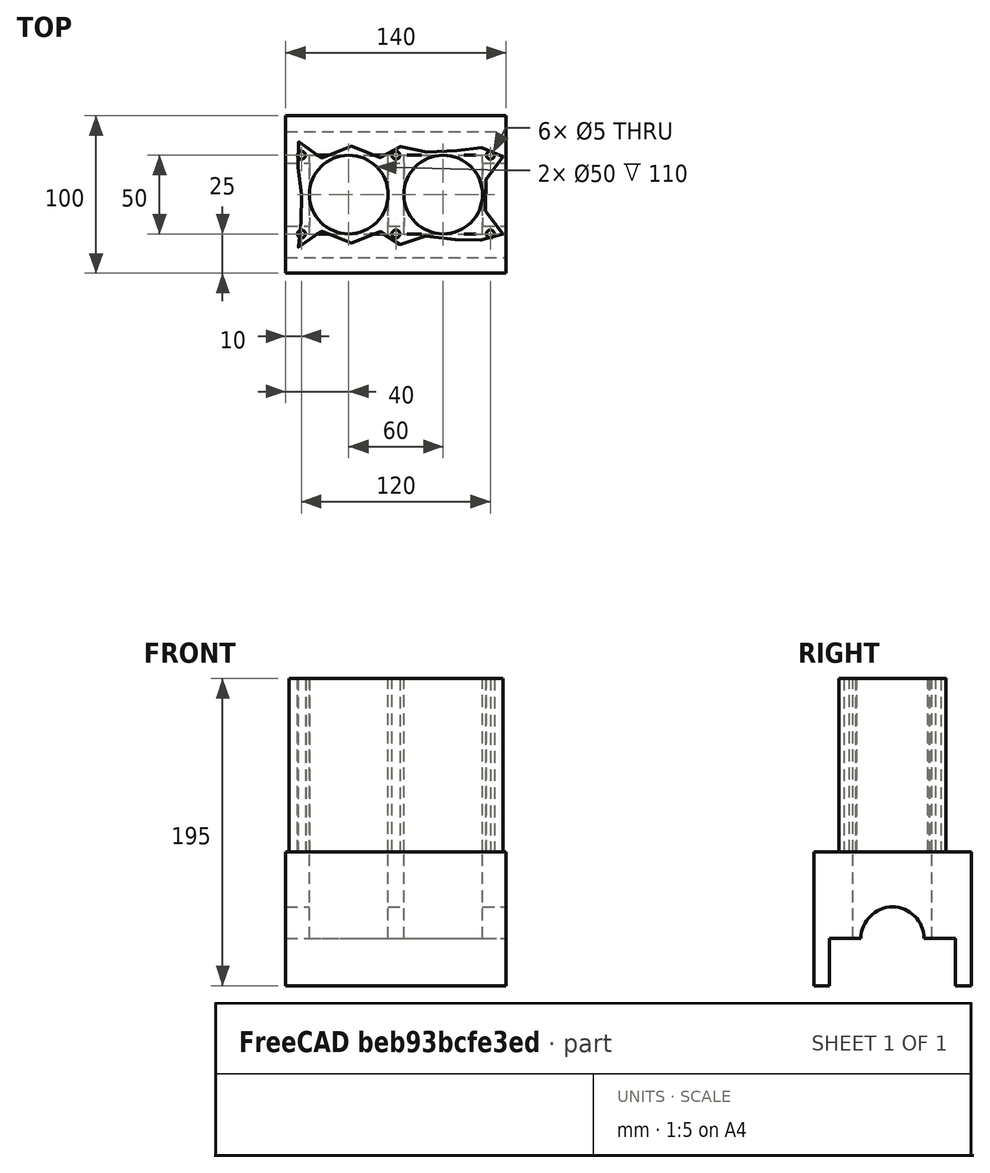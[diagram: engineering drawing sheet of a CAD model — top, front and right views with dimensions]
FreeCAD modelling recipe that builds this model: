
FCSTD DOCUMENT  (FreeCAD 0.19R17171 (Git))
Label: EngineBlock
License: Creative Commons Attribution-ShareAlike
LicenseURL: https://creativecommons.org/licenses/by-sa/4.0/
objects: Part::Part2DObjectPython×8, Part::Extrusion×7, Part::Box×5, Part::Cut×5, Part::Cylinder×3, Part::MultiFuse×3, Part::Mirroring×3, App::DocumentObjectGroup×1, Part::MultiCommon×1
note: 35 computed .brp shape members not serialized (recipe doc carries the construction recipe); baked Part::Feature solids carry a one-line shape summary decoded from their .brp

FEATURE [Part::Box] Box  label="Billet"
  AttacherType = Attacher::AttachEngine3D
  Height = 110
  Length = 140
  Placement = pos=(0,-40,0) rot=(0,0,1;0rad)
  Width = 80
FEATURE [Part::Cylinder] Cylinder  label="Cylinder 1"
  Angle = 360
  AttacherType = Attacher::AttachEngine3D
  Height = 110
  Placement = pos=(40,0,0) rot=(0,0,1;0rad)
  Radius = 25
FEATURE [Part::Cylinder] Cylinder001  label="Cylinder 2"
  Angle = 360
  AttacherType = Attacher::AttachEngine3D
  Height = 110
  Placement = pos=(100,0,0) rot=(0,0,1;0rad)
  Radius = 25
FEATURE [Part::MultiFuse] Fusion  label="Cylinders"
  Shapes = -> [Cylinder,Cylinder001]
FEATURE [Part::Cut] Cut  label="Bored Block"
  Base = -> Box
  Tool = -> Fusion
FEATURE [Part::Box] Box001  label="Crankcase Billet"
  AttacherType = Attacher::AttachEngine3D
  Height = 85
  Length = 140
  Placement = pos=(0,-50,-85) rot=(0,0,1;0rad)
  Width = 100
FEATURE [Part::Box] Box002  label="Bearing carve"
  AttacherType = Attacher::AttachEngine3D
  Height = 30
  Length = 140
  Placement = pos=(0,-40,-85) rot=(0,0,1;0rad)
  Width = 80
FEATURE [Part::Cut] Cut001  label="Carved crankcase"
  Base = -> Box001
  Tool = -> Box002
FEATURE [Part::Cylinder] Cylinder002  label="Cranshaft carve"
  Angle = 360
  AttacherType = Attacher::AttachEngine3D
  Height = 140
  Placement = pos=(0,0,-55) rot=(0,1,0;1.5708rad)
  Radius = 20
FEATURE [Part::Cut] Cut002  label="Crankcase with journals"
  Base = -> Cut001
  Tool = -> Cylinder002
FEATURE [Part::Box] Box003  label="Box carve 1"
  AttacherType = Attacher::AttachEngine3D
  Height = 55
  Length = 50
  Placement = pos=(15,-25,-55) rot=(0,0,1;0rad)
  Width = 50
FEATURE [Part::Box] Box004  label="Box carve 2"
  AttacherType = Attacher::AttachEngine3D
  Height = 55
  Length = 50
  Placement = pos=(75,-25,-55) rot=(0,0,1;0rad)
  Width = 50
FEATURE [Part::MultiFuse] Fusion001  label="Box carvers"
  Shapes = -> [Box003,Box004]
FEATURE [Part::Cut] Cut003  label="Crankcase"
  Base = -> Cut002
  Tool = -> Fusion001
FEATURE [Part::Part2DObjectPython] Circle003  label="Bolt 007"  # Draft 2D object (typed FeaturePython)
  FirstAngle = 0
  LastAngle = 0
  MapMode = 5
  Placement = pos=(10,25,110) rot=(0,0,1;0rad)
  Radius = 2.5
FEATURE [Part::Mirroring] Part__Mirroring  label="Bolt 4"
  Base = (0,0,0)
  Normal = (0,1,0)
  Source = -> Circle003
FEATURE [Part::Extrusion] Extrude  label="Head bolt bore 1"
  Base = -> Circle003
  Dir = (0,0,-110)
  DirMode = 0
  FaceMakerClass = Part::FaceMakerExtrusion
  LengthFwd = 0
  LengthRev = 0
  Solid = false
  Symmetric = false
FEATURE [Part::Extrusion] Extrude003  label="Head bolt bore 4"
  Base = -> Part__Mirroring
  Dir = (0,0,-110)
  DirMode = 0
  FaceMakerClass = Part::FaceMakerExtrusion
  LengthFwd = 0
  LengthRev = 0
  Solid = false
  Symmetric = false
FEATURE [Part::Part2DObjectPython] Circle004  label="Bolt 008"  # Draft 2D object (typed FeaturePython)
  FirstAngle = 0
  LastAngle = 0
  MapMode = 5
  Placement = pos=(70,25,110) rot=(0,0,1;0rad)
  Radius = 2.5
FEATURE [Part::Mirroring] Part__Mirroring001  label="Bolt 5"
  Base = (0,0,0)
  Normal = (0,1,0)
  Source = -> Circle004
FEATURE [Part::Extrusion] Extrude001  label="Head bolt bore 2"
  Base = -> Circle004
  Dir = (0,0,-110)
  DirMode = 0
  FaceMakerClass = Part::FaceMakerExtrusion
  LengthFwd = 0
  LengthRev = 0
  Solid = false
  Symmetric = false
FEATURE [Part::Extrusion] Extrude004  label="Head bolt bore 5"
  Base = -> Part__Mirroring001
  Dir = (0,0,-110)
  DirMode = 0
  FaceMakerClass = Part::FaceMakerExtrusion
  LengthFwd = 0
  LengthRev = 0
  Solid = false
  Symmetric = false
FEATURE [Part::Part2DObjectPython] Circle005  label="Bolt 009"  # Draft 2D object (typed FeaturePython)
  FirstAngle = 0
  LastAngle = 0
  MapMode = 5
  Placement = pos=(130,25,110) rot=(0,0,1;0rad)
  Radius = 2.5
FEATURE [Part::Mirroring] Part__Mirroring002  label="Bolt 6"
  Base = (0,0,0)
  Normal = (0,1,0)
  Source = -> Circle005
FEATURE [Part::Extrusion] Extrude002  label="Head bolt bore 3"
  Base = -> Circle005
  Dir = (0,0,-110)
  DirMode = 0
  FaceMakerClass = Part::FaceMakerExtrusion
  LengthFwd = 0
  LengthRev = 0
  Solid = false
  Symmetric = false
FEATURE [Part::Extrusion] Extrude005  label="Head bolt bore 6"
  Base = -> Part__Mirroring002
  Dir = (0,0,-110)
  DirMode = 0
  FaceMakerClass = Part::FaceMakerExtrusion
  LengthFwd = 0
  LengthRev = 0
  Solid = false
  Symmetric = false
FEATURE [Part::MultiFuse] Fusion002  label="Head bolt boreholes"
  Shapes = -> [Extrude,Extrude001,Extrude002,Extrude003,Extrude004,Extrude005]
FEATURE [Part::Cut] Cut004  label="Block with headbolts"
  Base = -> Cut
  Tool = -> Fusion002
FEATURE [Part::Part2DObjectPython] Polygon004  # Draft 2D object (typed FeaturePython)
  ChamferSize = 0
  DrawMode = 0
  FacesNumber = 14
  FilletRadius = 0
  MapMode = 5
  Placement = pos=(40,0,110) rot=(0,0,1;0rad)
  Radius = 30
FEATURE [Part::Part2DObjectPython] Polygon005  # Draft 2D object (typed FeaturePython)
  ChamferSize = 0
  DrawMode = 0
  FacesNumber = 14
  FilletRadius = 0
  MapMode = 5
  Placement = pos=(100,0,110) rot=(0,0,1;0rad)
  Radius = 30
FEATURE [Part::Part2DObjectPython] Polygon006  # Draft 2D object (typed FeaturePython)
  ChamferSize = 0
  DrawMode = 0
  FacesNumber = 22
  FilletRadius = 0
  MapMode = 5
  Placement = pos=(40,0,110) rot=(0,0,1;0rad)
  Radius = 45
FEATURE [Part::Part2DObjectPython] Polygon007  # Draft 2D object (typed FeaturePython)
  ChamferSize = 0
  DrawMode = 0
  FacesNumber = 22
  FilletRadius = 0
  MapMode = 5
  Placement = pos=(100,0,110) rot=(0,0,1;0rad)
  Radius = 45
FEATURE [App::DocumentObjectGroup] Construction
  Group = -> [Polygon004,Polygon005,Polygon006,Polygon007]
FEATURE [Part::Part2DObjectPython] BSpline001  # Draft 2D object (typed FeaturePython)
  Closed = true
  MapMode = 5
  Points = (36) [(10,2.75536e-15,110),(12.9709,13.0165,110),(2.14359,24.3288,110),(10.5313,34.0087,110),(21.2953,23.4549,110),(33.3244,29.2478,110),+30 more]
FEATURE [Part::Extrusion] Extrude006  label="Extruded spline"
  Base = -> BSpline001
  Dir = (0,0,-110)
  DirMode = 0
  FaceMakerClass = Part::FaceMakerExtrusion
  LengthFwd = 0
  LengthRev = 0
  Solid = false
  Symmetric = false
FEATURE [Part::MultiCommon] Common  label="Engine block"
  Shapes = -> [Extrude006,Cut004]
